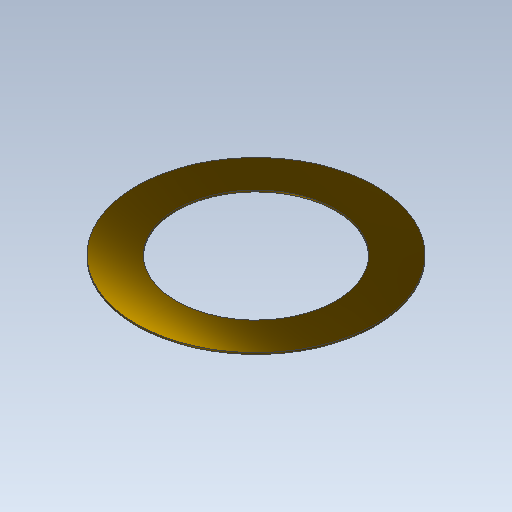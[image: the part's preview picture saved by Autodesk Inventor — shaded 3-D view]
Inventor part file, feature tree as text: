
AUTODESK INVENTOR PART (.ipt)
format: ipt  version: 2020.3 (Build 243373000, 373)  size: 113,664 bytes
history: native  units: mm
features: hole x1, extrude x1, sketch x1
ambient origin geometry x8: Origin, YZ Plane, XZ Plane, XY Plane, X Axis, Y Axis, Z Axis, Center Point
bodies: Solid1 (feature_tree)
feature tree (3):
  hole  "hole_plating"  [1 undecoded]
  extrude  "Extrusion1"  Depth=0.01mm TaperAngle=0.0deg
  sketch  "Sketch1"  dims[d0=1.0mm d1=1.5mm d2=0.01mm d3=0.0mm]
note: 1 required parameter value undecoded (feature->parameter linkage not recoverable at this tier; creation-order binding heuristic only, values carry confidence <= 0.55)
